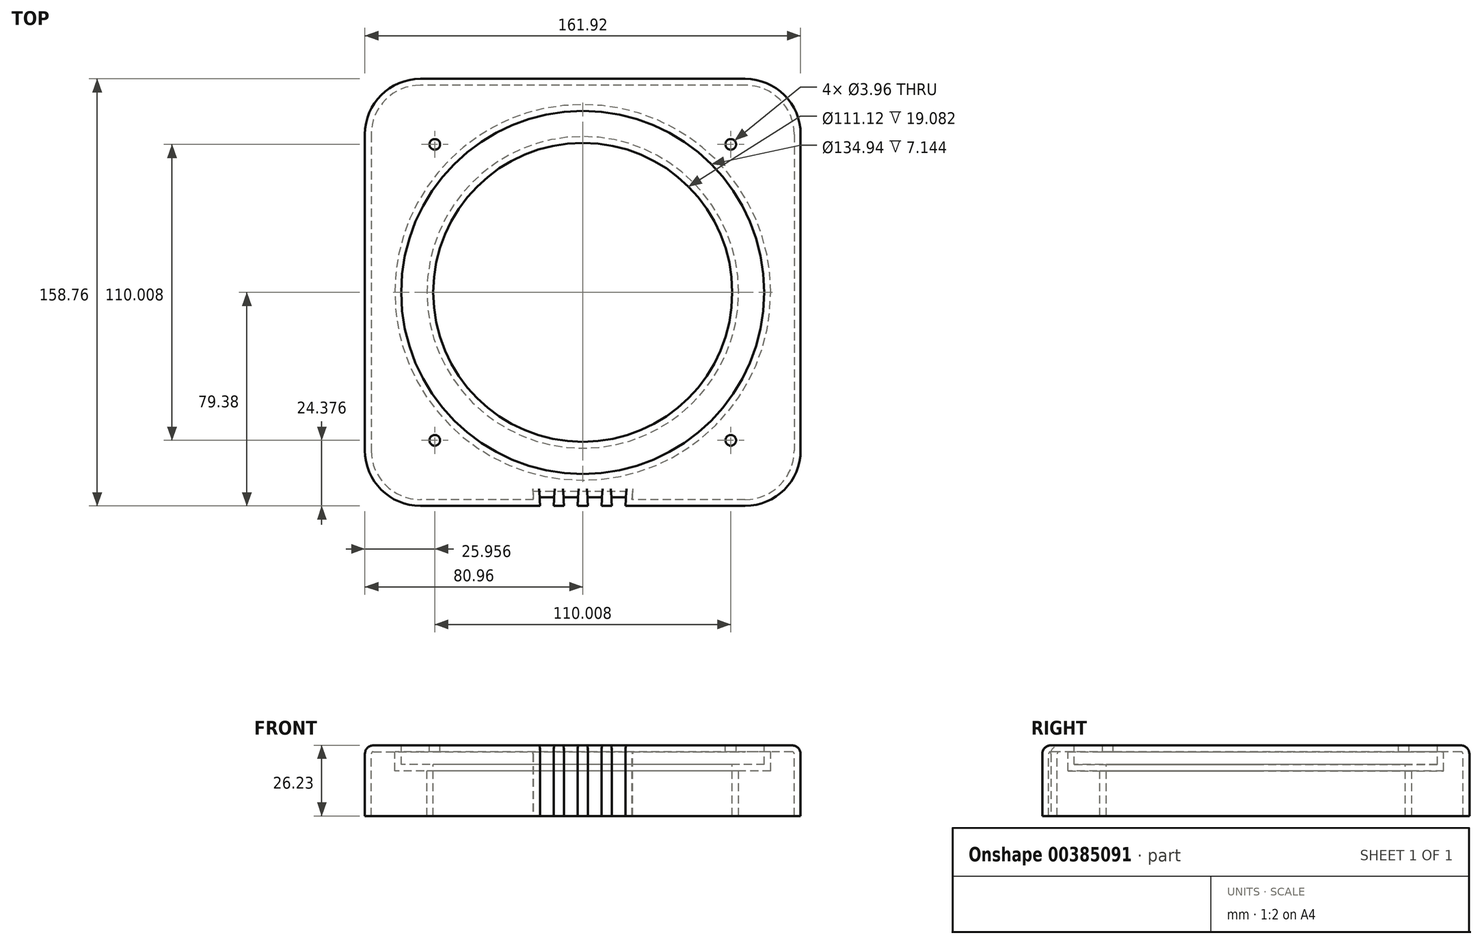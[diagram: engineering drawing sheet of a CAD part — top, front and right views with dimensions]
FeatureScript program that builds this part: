
annotation { "Feature Type Name" : "Feature", "Feature Type Description" : "" }
export const myFeature = defineFeature(function(context is Context, id is Id, definition is map)
    precondition{}
    {
        {
            var Q0;
            Q0=qCreatedBy(makeId("Top.planeOp"),FACE);
            var sketch = newSketch(context, id + "F0", { "sketchPlane" : qUnion([Q0])});
            skLineSegment(sketch, "E0.bottom", {"start": v(60.34, 79.38) * mm, "end": v(-60.34, 79.38) * mm});
            skLineSegment(sketch, "E0.top", {"start": v(60.34, -79.38) * mm, "end": v(-60.34, -79.38) * mm});
            skLineSegment(sketch, "E0.left", {"start": v(80.96, 58.75) * mm, "end": v(80.96, -58.75) * mm});
            skLineSegment(sketch, "E0.right", {"start": v(-80.96, 58.75) * mm, "end": v(-80.96, -58.75) * mm});
            skPoint(sketch, "E0.middle", {"position": v(0, 0) * mm});
            skPoint(sketch, "E1.visualSharp", {"position": v(-80.96, 79.38) * mm});
            skArc(sketch, "E1.filletArc", {"start": v(-60.34, 79.38) * mm, "mid": v(-74.92, 73.33) * mm, "end": v(-80.96, 58.75) * mm});
            skPoint(sketch, "E2.visualSharp", {"position": v(80.96, 79.38) * mm});
            skArc(sketch, "E2.filletArc", {"start": v(80.96, 58.75) * mm, "mid": v(74.92, 73.33) * mm, "end": v(60.34, 79.38) * mm});
            skPoint(sketch, "E3.visualSharp", {"position": v(80.96, -79.38) * mm});
            skArc(sketch, "E3.filletArc", {"start": v(60.34, -79.38) * mm, "mid": v(74.92, -73.33) * mm, "end": v(80.96, -58.75) * mm});
            skPoint(sketch, "E4.visualSharp", {"position": v(-80.96, -79.38) * mm});
            skArc(sketch, "E4.filletArc", {"start": v(-80.96, -58.75) * mm, "mid": v(-74.92, -73.33) * mm, "end": v(-60.34, -79.38) * mm});
            skCircle(sketch, "E5", {"center": v(0, 0) * mm, "radius": 55.56 * mm});
            skCircle(sketch, "E6", {"center": v(0, 0) * mm, "radius": 67.47 * mm});
            skCircle(sketch, "E7", {"center": v(55, 55) * mm, "radius": 1.98 * mm});
            skCircle(sketch, "E8", {"center": v(55, -55) * mm, "radius": 1.98 * mm});
            skCircle(sketch, "E9", {"center": v(-55, -55) * mm, "radius": 1.98 * mm});
            skCircle(sketch, "E10", {"center": v(-55, 55) * mm, "radius": 1.98 * mm});
            skSolve(sketch);
        }
        {
            var Q0;
            Q0=makeQuery(id+"F0.imprint","IMPRINT",FACE,{"disambiguationData":[TD([[makeQuery(id+"F0.imprint","IMPRINT",EDGE,{"derivedFrom":sQuery(id+"F0.wireOp",EDGE,"E0.bottom")}),1.0]])]});
            var Q1;
            Q1=makeQuery(id+"F0.imprint","IMPRINT",FACE,{"disambiguationData":[TD([[makeQuery(id+"F0.imprint","IMPRINT",EDGE,{"derivedFrom":sQuery(id+"F0.wireOp",EDGE,"E5")}),-1.0]])]});
            extrude(context, id + "F1", {"entities" : qUnion([Q0, Q1]), "oppositeDirection" : true, "depth" : 26.23 * mm});
        }
        {
            var Q0;
            Q0=makeQuery(id+"F1.opExtrude","SWEPT_FACE",FACE,{"disambiguationData":[OSD([sQuery(id+"F0.wireOp",EDGE,"E0.top")])]});
            var sketch = newSketch(context, id + "F2", { "sketchPlane" : qUnion([Q0])});
            skLineSegment(sketch, "E11.bottom", {"start": v(1.9, -31.75) * mm, "end": v(-1.9, -31.75) * mm});
            skLineSegment(sketch, "E11.top", {"start": v(1.9, 31.75) * mm, "end": v(-1.9, 31.75) * mm});
            skLineSegment(sketch, "E11.left", {"start": v(1.9, -31.75) * mm, "end": v(1.9, 31.75) * mm});
            skLineSegment(sketch, "E11.right", {"start": v(-1.9, -31.75) * mm, "end": v(-1.9, 31.75) * mm});
            skPoint(sketch, "E11.middle", {"position": v(0, 0) * mm});
            skLineSegment(sketch, "E12.1.0.0", {"start": v(6.98, -31.75) * mm, "end": v(6.99, 31.75) * mm});
            skLineSegment(sketch, "E12.1.0.1", {"start": v(10.8, 31.75) * mm, "end": v(6.99, 31.75) * mm});
            skLineSegment(sketch, "E12.1.0.2", {"start": v(10.8, -31.75) * mm, "end": v(10.8, 31.75) * mm});
            skLineSegment(sketch, "E12.1.0.3", {"start": v(10.8, -31.75) * mm, "end": v(6.98, -31.75) * mm});
            skLineSegment(sketch, "E12.direction1", {"start": v(-1.9, -31.75) * mm, "end": v(6.98, -31.75) * mm, "construction": true});
            skLineSegment(sketch, "E13.0.2.0", {"start": v(15.87, -31.75) * mm, "end": v(15.88, 31.75) * mm});
            skLineSegment(sketch, "E13.3.2.0", {"start": v(19.69, 31.75) * mm, "end": v(15.88, 31.75) * mm});
            skLineSegment(sketch, "E13.6.2.0", {"start": v(19.68, -31.75) * mm, "end": v(19.69, 31.75) * mm});
            skLineSegment(sketch, "E13.9.2.0", {"start": v(19.68, -31.75) * mm, "end": v(15.88, -31.75) * mm});
            skLineSegment(sketch, "E14.MirrorCS", {"start": v(-19.68, -31.75) * mm, "end": v(-15.88, -31.75) * mm});
            skLineSegment(sketch, "E15.MirrorCS", {"start": v(-10.8, -31.75) * mm, "end": v(-6.98, -31.75) * mm});
            skLineSegment(sketch, "E16.MirrorCS", {"start": v(-19.69, 31.75) * mm, "end": v(-15.88, 31.75) * mm});
            skLineSegment(sketch, "E17.MirrorCS", {"start": v(-10.8, 31.75) * mm, "end": v(-6.99, 31.75) * mm});
            skLineSegment(sketch, "E18.MirrorCS", {"start": v(-10.8, -31.75) * mm, "end": v(-10.8, 31.75) * mm});
            skLineSegment(sketch, "E19.MirrorCS", {"start": v(-19.68, -31.75) * mm, "end": v(-19.69, 31.75) * mm});
            skLineSegment(sketch, "E20.MirrorCS", {"start": v(-15.87, -31.75) * mm, "end": v(-15.88, 31.75) * mm});
            skLineSegment(sketch, "E21.MirrorCS", {"start": v(-6.98, -31.75) * mm, "end": v(-6.99, 31.75) * mm});
            skSolve(sketch);
        }
        {
            var Q0;
            Q0=makeQuery(id+"F0.imprint","IMPRINT",FACE,{"disambiguationData":[TD([[makeQuery(id+"F0.imprint","IMPRINT",EDGE,{"derivedFrom":sQuery(id+"F0.wireOp",EDGE,"E5")}),-1.0]])]});
            extrude(context, id + "F3", {"entities" : qUnion([Q0]), "operationType" : NewBodyOperationType.REMOVE, "oppositeDirection" : true, "depth" : 7.14 * mm});
        }
        {
            var Q0;
            {var subQ0=sQuery(id+"F2.wireOp",EDGE,"E18.MirrorCS");var subQ1=sQuery(id+"F0.wireOp",EDGE,"E0.top");var subQ2=makeQuery(id+"F1.opExtrude","CAP_EDGE",EDGE,{"disambiguationData":[OSD([subQ1])],"isStart":false});var subQ3=makeQuery(id+"F2.imprint","INTERSECT",VERTEX,{"derivedFrom":[subQ2,subQ0]});Q0=makeQuery(id+"F2.imprint","IMPRINT",FACE,{"disambiguationData":[TD([[makeQuery(id+"F2.imprint","IMPRINT",EDGE,{"disambiguationData":[TD([[subQ3,-1.0]])],"derivedFrom":subQ2}),-1.0]])]});}
            var Q1;
            {var subQ0=sQuery(id+"F2.wireOp",EDGE,"E11.right");var subQ1=sQuery(id+"F0.wireOp",EDGE,"E0.top");var subQ2=makeQuery(id+"F1.opExtrude","CAP_EDGE",EDGE,{"disambiguationData":[OSD([subQ1])],"isStart":false});var subQ3=makeQuery(id+"F2.imprint","INTERSECT",VERTEX,{"derivedFrom":[subQ2,subQ0]});Q1=makeQuery(id+"F2.imprint","IMPRINT",FACE,{"disambiguationData":[TD([[makeQuery(id+"F2.imprint","IMPRINT",EDGE,{"disambiguationData":[TD([[subQ3,-1.0]])],"derivedFrom":subQ2}),-1.0]])]});}
            var Q2;
            {var subQ0=sQuery(id+"F2.wireOp",EDGE,"E11.left");var subQ1=sQuery(id+"F0.wireOp",EDGE,"E0.top");var subQ2=makeQuery(id+"F1.opExtrude","CAP_EDGE",EDGE,{"disambiguationData":[OSD([subQ1])],"isStart":false});var subQ3=makeQuery(id+"F2.imprint","INTERSECT",VERTEX,{"derivedFrom":[subQ2,subQ0]});Q2=makeQuery(id+"F2.imprint","IMPRINT",FACE,{"disambiguationData":[TD([[makeQuery(id+"F2.imprint","IMPRINT",EDGE,{"disambiguationData":[TD([[subQ3,1.0]])],"derivedFrom":subQ2}),-1.0]])]});}
            var Q3;
            {var subQ0=sQuery(id+"F2.wireOp",EDGE,"E12.1.0.2");var subQ1=sQuery(id+"F0.wireOp",EDGE,"E0.top");var subQ2=makeQuery(id+"F1.opExtrude","CAP_EDGE",EDGE,{"disambiguationData":[OSD([subQ1])],"isStart":false});var subQ3=makeQuery(id+"F2.imprint","INTERSECT",VERTEX,{"derivedFrom":[subQ2,subQ0]});Q3=makeQuery(id+"F2.imprint","IMPRINT",FACE,{"disambiguationData":[TD([[makeQuery(id+"F2.imprint","IMPRINT",EDGE,{"disambiguationData":[TD([[subQ3,1.0]])],"derivedFrom":subQ2}),-1.0]])]});}
            extrude(context, id + "F4", {"entities" : qUnion([Q0, Q1, Q2, Q3]), "operationType" : NewBodyOperationType.REMOVE, "oppositeDirection" : true, "depth" : 3.17 * mm, "hasDraft" : true, "draftAngle" : 3 * degree});
        }
        {
            var Q0;
            Q0=makeQuery(id+"F1.opExtrude","CAP_EDGE",EDGE,{"disambiguationData":[OSD([sQuery(id+"F0.wireOp",EDGE,"E2.filletArc")])],"isStart":true});
            var Q1;
            Q1=makeQuery(id+"F1.opExtrude","CAP_EDGE",EDGE,{"disambiguationData":[OSD([sQuery(id+"F0.wireOp",EDGE,"E3.filletArc")])],"isStart":true});
            var Q2;
            Q2=makeQuery(id+"F1.opExtrude","CAP_EDGE",EDGE,{"disambiguationData":[OSD([sQuery(id+"F0.wireOp",EDGE,"E4.filletArc")])],"isStart":true});
            var Q3;
            Q3=makeQuery(id+"F1.opExtrude","CAP_EDGE",EDGE,{"disambiguationData":[OSD([sQuery(id+"F0.wireOp",EDGE,"E1.filletArc")])],"isStart":true});
            var Q4;
            {var subQ0=sQuery(id+"F0.wireOp",EDGE,"E0.top");var subQ1=makeQuery(id+"F1.opExtrude","CAP_EDGE",EDGE,{"disambiguationData":[OSD([subQ0])],"isStart":true});Q4=makeQuery(id+"F4.boolean.opBoolean","COPY",EDGE,{"derivedFrom":makeQuery(id+"F4.opExtrude","CAP_EDGE",EDGE,{"disambiguationData":[OSD([subQ0]),TDD([makeQuery(id+"F2.imprint","IMPRINT",EDGE,{"disambiguationData":[TD([[makeQuery(id+"F2.imprint","INTERSECT",VERTEX,{"derivedFrom":[subQ1,sQuery(id+"F2.wireOp",EDGE,"E18.MirrorCS")]}),-1.0]])],"derivedFrom":subQ1})])],"isStart":false})});}
            var Q5;
            {var subQ0=sQuery(id+"F0.wireOp",EDGE,"E0.top");Q5=makeQuery(id+"F4.boolean.opBoolean","SPLIT",EDGE,{"disambiguationData":[TD([makeQuery(id+"F4.opExtrude","SWEPT_FACE",FACE,{"disambiguationData":[OSD([sQuery(id+"F2.wireOp",EDGE,"E18.MirrorCS")])]})])],"derivedFrom":makeQuery(id+"F1.opExtrude","CAP_EDGE",EDGE,{"disambiguationData":[OSD([subQ0])],"isStart":true})});}
            var Q6;
            {var subQ0=sQuery(id+"F0.wireOp",EDGE,"E0.top");var subQ1=makeQuery(id+"F1.opExtrude","CAP_EDGE",EDGE,{"disambiguationData":[OSD([subQ0])],"isStart":true});Q6=makeQuery(id+"F4.boolean.opBoolean","COPY",EDGE,{"derivedFrom":makeQuery(id+"F4.opExtrude","CAP_EDGE",EDGE,{"disambiguationData":[OSD([subQ0]),TDD([makeQuery(id+"F2.imprint","IMPRINT",EDGE,{"disambiguationData":[TD([[makeQuery(id+"F2.imprint","INTERSECT",VERTEX,{"derivedFrom":[subQ1,sQuery(id+"F2.wireOp",EDGE,"E11.right")]}),-1.0]])],"derivedFrom":subQ1})])],"isStart":false})});}
            var Q7;
            {var subQ0=sQuery(id+"F0.wireOp",EDGE,"E0.top");Q7=makeQuery(id+"F4.boolean.opBoolean","SPLIT",EDGE,{"disambiguationData":[TD([makeQuery(id+"F4.opExtrude","SWEPT_FACE",FACE,{"disambiguationData":[OSD([sQuery(id+"F2.wireOp",EDGE,"E11.left")])]})])],"derivedFrom":makeQuery(id+"F1.opExtrude","CAP_EDGE",EDGE,{"disambiguationData":[OSD([subQ0])],"isStart":true})});}
            var Q8;
            {var subQ0=sQuery(id+"F0.wireOp",EDGE,"E0.top");var subQ1=makeQuery(id+"F1.opExtrude","CAP_EDGE",EDGE,{"disambiguationData":[OSD([subQ0])],"isStart":true});Q8=makeQuery(id+"F4.boolean.opBoolean","COPY",EDGE,{"derivedFrom":makeQuery(id+"F4.opExtrude","CAP_EDGE",EDGE,{"disambiguationData":[OSD([subQ0]),TDD([makeQuery(id+"F2.imprint","IMPRINT",EDGE,{"disambiguationData":[TD([[makeQuery(id+"F2.imprint","INTERSECT",VERTEX,{"derivedFrom":[subQ1,sQuery(id+"F2.wireOp",EDGE,"E11.left")]}),1.0]])],"derivedFrom":subQ1})])],"isStart":false})});}
            var Q9;
            {var subQ0=sQuery(id+"F0.wireOp",EDGE,"E0.top");Q9=makeQuery(id+"F4.boolean.opBoolean","SPLIT",EDGE,{"disambiguationData":[TD([makeQuery(id+"F4.opExtrude","SWEPT_FACE",FACE,{"disambiguationData":[OSD([sQuery(id+"F2.wireOp",EDGE,"E12.1.0.0")])]})])],"derivedFrom":makeQuery(id+"F1.opExtrude","CAP_EDGE",EDGE,{"disambiguationData":[OSD([subQ0])],"isStart":true})});}
            var Q10;
            {var subQ0=sQuery(id+"F0.wireOp",EDGE,"E0.top");var subQ1=makeQuery(id+"F1.opExtrude","CAP_EDGE",EDGE,{"disambiguationData":[OSD([subQ0])],"isStart":true});Q10=makeQuery(id+"F4.boolean.opBoolean","COPY",EDGE,{"derivedFrom":makeQuery(id+"F4.opExtrude","CAP_EDGE",EDGE,{"disambiguationData":[OSD([subQ0]),TDD([makeQuery(id+"F2.imprint","IMPRINT",EDGE,{"disambiguationData":[TD([[makeQuery(id+"F2.imprint","INTERSECT",VERTEX,{"derivedFrom":[subQ1,sQuery(id+"F2.wireOp",EDGE,"E12.1.0.2")]}),1.0]])],"derivedFrom":subQ1})])],"isStart":false})});}
            var Q11;
            {var subQ0=sQuery(id+"F0.wireOp",EDGE,"E0.top");Q11=makeQuery(id+"F4.boolean.opBoolean","INTERSECT",EDGE,{"derivedFrom":[makeQuery(id+"F1.opExtrude","CAP_FACE",FACE,{"disambiguationData":[OSD([sQuery(id+"F0.wireOp",EDGE,"E0.bottom"),subQ0,sQuery(id+"F0.wireOp",EDGE,"E0.left"),sQuery(id+"F0.wireOp",EDGE,"E0.right"),sQuery(id+"F0.wireOp",EDGE,"E1.filletArc"),sQuery(id+"F0.wireOp",EDGE,"E2.filletArc"),sQuery(id+"F0.wireOp",EDGE,"E3.filletArc"),sQuery(id+"F0.wireOp",EDGE,"E4.filletArc"),sQuery(id+"F0.wireOp",EDGE,"E5"),sQuery(id+"F0.wireOp",EDGE,"E7"),sQuery(id+"F0.wireOp",EDGE,"E8"),sQuery(id+"F0.wireOp",EDGE,"E9"),sQuery(id+"F0.wireOp",EDGE,"E10")])],"isStart":true}),makeQuery(id+"F4.opExtrude","CAP_FACE",FACE,{"disambiguationData":[OSD([subQ0,sQuery(id+"F2.wireOp",EDGE,"E18.MirrorCS"),sQuery(id+"F2.wireOp",EDGE,"E20.MirrorCS")])],"isStart":false})]});}
            var Q12;
            {var subQ0=sQuery(id+"F0.wireOp",EDGE,"E0.top");Q12=makeQuery(id+"F4.boolean.opBoolean","INTERSECT",EDGE,{"derivedFrom":[makeQuery(id+"F1.opExtrude","CAP_FACE",FACE,{"disambiguationData":[OSD([sQuery(id+"F0.wireOp",EDGE,"E0.bottom"),subQ0,sQuery(id+"F0.wireOp",EDGE,"E0.left"),sQuery(id+"F0.wireOp",EDGE,"E0.right"),sQuery(id+"F0.wireOp",EDGE,"E1.filletArc"),sQuery(id+"F0.wireOp",EDGE,"E2.filletArc"),sQuery(id+"F0.wireOp",EDGE,"E3.filletArc"),sQuery(id+"F0.wireOp",EDGE,"E4.filletArc"),sQuery(id+"F0.wireOp",EDGE,"E5"),sQuery(id+"F0.wireOp",EDGE,"E7"),sQuery(id+"F0.wireOp",EDGE,"E8"),sQuery(id+"F0.wireOp",EDGE,"E9"),sQuery(id+"F0.wireOp",EDGE,"E10")])],"isStart":true}),makeQuery(id+"F4.opExtrude","CAP_FACE",FACE,{"disambiguationData":[OSD([subQ0,sQuery(id+"F2.wireOp",EDGE,"E11.right"),sQuery(id+"F2.wireOp",EDGE,"E21.MirrorCS")])],"isStart":false})]});}
            var Q13;
            {var subQ0=sQuery(id+"F0.wireOp",EDGE,"E0.top");Q13=makeQuery(id+"F4.boolean.opBoolean","INTERSECT",EDGE,{"derivedFrom":[makeQuery(id+"F1.opExtrude","CAP_FACE",FACE,{"disambiguationData":[OSD([sQuery(id+"F0.wireOp",EDGE,"E0.bottom"),subQ0,sQuery(id+"F0.wireOp",EDGE,"E0.left"),sQuery(id+"F0.wireOp",EDGE,"E0.right"),sQuery(id+"F0.wireOp",EDGE,"E1.filletArc"),sQuery(id+"F0.wireOp",EDGE,"E2.filletArc"),sQuery(id+"F0.wireOp",EDGE,"E3.filletArc"),sQuery(id+"F0.wireOp",EDGE,"E4.filletArc"),sQuery(id+"F0.wireOp",EDGE,"E5"),sQuery(id+"F0.wireOp",EDGE,"E7"),sQuery(id+"F0.wireOp",EDGE,"E8"),sQuery(id+"F0.wireOp",EDGE,"E9"),sQuery(id+"F0.wireOp",EDGE,"E10")])],"isStart":true}),makeQuery(id+"F4.opExtrude","CAP_FACE",FACE,{"disambiguationData":[OSD([subQ0,sQuery(id+"F2.wireOp",EDGE,"E11.left"),sQuery(id+"F2.wireOp",EDGE,"E12.1.0.0")])],"isStart":false})]});}
            var Q14;
            {var subQ0=sQuery(id+"F0.wireOp",EDGE,"E0.top");Q14=makeQuery(id+"F4.boolean.opBoolean","INTERSECT",EDGE,{"derivedFrom":[makeQuery(id+"F1.opExtrude","CAP_FACE",FACE,{"disambiguationData":[OSD([sQuery(id+"F0.wireOp",EDGE,"E0.bottom"),subQ0,sQuery(id+"F0.wireOp",EDGE,"E0.left"),sQuery(id+"F0.wireOp",EDGE,"E0.right"),sQuery(id+"F0.wireOp",EDGE,"E1.filletArc"),sQuery(id+"F0.wireOp",EDGE,"E2.filletArc"),sQuery(id+"F0.wireOp",EDGE,"E3.filletArc"),sQuery(id+"F0.wireOp",EDGE,"E4.filletArc"),sQuery(id+"F0.wireOp",EDGE,"E5"),sQuery(id+"F0.wireOp",EDGE,"E7"),sQuery(id+"F0.wireOp",EDGE,"E8"),sQuery(id+"F0.wireOp",EDGE,"E9"),sQuery(id+"F0.wireOp",EDGE,"E10")])],"isStart":true}),makeQuery(id+"F4.opExtrude","CAP_FACE",FACE,{"disambiguationData":[OSD([subQ0,sQuery(id+"F2.wireOp",EDGE,"E12.1.0.2"),sQuery(id+"F2.wireOp",EDGE,"E13.0.2.0")])],"isStart":false})]});}
            fillet(context, id + "F5", {"entities" : qUnion([Q0, Q1, Q2, Q3, Q4, Q5, Q6, Q7, Q8, Q9, Q10, Q11, Q12, Q13, Q14]), "radius" : 3.17 * mm, "tangentPropagation" : true, "allowEdgeOverflow" : false});
        }
        {
            var Q0;
            Q0=makeQuery(id+"F1.opExtrude","CAP_FACE",FACE,{"disambiguationData":[OSD([sQuery(id+"F0.wireOp",EDGE,"E0.bottom"),sQuery(id+"F0.wireOp",EDGE,"E0.top"),sQuery(id+"F0.wireOp",EDGE,"E0.left"),sQuery(id+"F0.wireOp",EDGE,"E0.right"),sQuery(id+"F0.wireOp",EDGE,"E1.filletArc"),sQuery(id+"F0.wireOp",EDGE,"E2.filletArc"),sQuery(id+"F0.wireOp",EDGE,"E3.filletArc"),sQuery(id+"F0.wireOp",EDGE,"E4.filletArc"),sQuery(id+"F0.wireOp",EDGE,"E5"),sQuery(id+"F0.wireOp",EDGE,"E7"),sQuery(id+"F0.wireOp",EDGE,"E8"),sQuery(id+"F0.wireOp",EDGE,"E9"),sQuery(id+"F0.wireOp",EDGE,"E10")])],"isStart":false});
            shell(context, id + "F6", {"entities" : qUnion([Q0]), "thickness" : 2.36 * mm});
        }
        {
            var Q0;
            {var subQ0=sQuery(id+"F0.wireOp",EDGE,"E10");var subQ1=sQuery(id+"F0.wireOp",EDGE,"E9");var subQ2=sQuery(id+"F0.wireOp",EDGE,"E8");var subQ3=sQuery(id+"F0.wireOp",EDGE,"E7");var subQ4=sQuery(id+"F0.wireOp",EDGE,"E5");var subQ5=sQuery(id+"F0.wireOp",EDGE,"E4.filletArc");var subQ6=sQuery(id+"F0.wireOp",EDGE,"E3.filletArc");var subQ7=sQuery(id+"F0.wireOp",EDGE,"E2.filletArc");var subQ8=sQuery(id+"F0.wireOp",EDGE,"E1.filletArc");var subQ9=sQuery(id+"F0.wireOp",EDGE,"E0.right");var subQ10=sQuery(id+"F0.wireOp",EDGE,"E0.left");var subQ11=sQuery(id+"F0.wireOp",EDGE,"E0.top");var subQ12=sQuery(id+"F0.wireOp",EDGE,"E0.bottom");Q0=makeQuery(id+"F6.opShell","OFFSET_FACE",FACE,{"disambiguationData":[OSD([subQ12,subQ11,subQ10,subQ9,subQ8,subQ7,subQ6,subQ5,subQ4,subQ3,subQ2,subQ1,subQ0]),TDD([makeQuery(id+"F1.opExtrude","CAP_FACE",FACE,{"disambiguationData":[OSD([subQ12,subQ11,subQ10,subQ9,subQ8,subQ7,subQ6,subQ5,subQ4,subQ3,subQ2,subQ1,subQ0])],"isStart":false})]),OD(1.0)]});}
            var Q1;
            {var subQ0=sQuery(id+"F0.wireOp",EDGE,"E10");var subQ1=sQuery(id+"F0.wireOp",EDGE,"E9");var subQ2=sQuery(id+"F0.wireOp",EDGE,"E8");var subQ3=sQuery(id+"F0.wireOp",EDGE,"E7");var subQ4=sQuery(id+"F0.wireOp",EDGE,"E5");var subQ5=sQuery(id+"F0.wireOp",EDGE,"E4.filletArc");var subQ6=sQuery(id+"F0.wireOp",EDGE,"E3.filletArc");var subQ7=sQuery(id+"F0.wireOp",EDGE,"E2.filletArc");var subQ8=sQuery(id+"F0.wireOp",EDGE,"E1.filletArc");var subQ9=sQuery(id+"F0.wireOp",EDGE,"E0.right");var subQ10=sQuery(id+"F0.wireOp",EDGE,"E0.left");var subQ11=sQuery(id+"F0.wireOp",EDGE,"E0.top");var subQ12=sQuery(id+"F0.wireOp",EDGE,"E0.bottom");Q1=makeQuery(id+"F6.opShell","OFFSET_FACE",FACE,{"disambiguationData":[OSD([subQ12,subQ11,subQ10,subQ9,subQ8,subQ7,subQ6,subQ5,subQ4,subQ3,subQ2,subQ1,subQ0]),TDD([makeQuery(id+"F1.opExtrude","CAP_FACE",FACE,{"disambiguationData":[OSD([subQ12,subQ11,subQ10,subQ9,subQ8,subQ7,subQ6,subQ5,subQ4,subQ3,subQ2,subQ1,subQ0])],"isStart":false})]),OD(2.0)]});}
            var Q2;
            {var subQ0=sQuery(id+"F0.wireOp",EDGE,"E10");var subQ1=sQuery(id+"F0.wireOp",EDGE,"E9");var subQ2=sQuery(id+"F0.wireOp",EDGE,"E8");var subQ3=sQuery(id+"F0.wireOp",EDGE,"E7");var subQ4=sQuery(id+"F0.wireOp",EDGE,"E5");var subQ5=sQuery(id+"F0.wireOp",EDGE,"E4.filletArc");var subQ6=sQuery(id+"F0.wireOp",EDGE,"E3.filletArc");var subQ7=sQuery(id+"F0.wireOp",EDGE,"E2.filletArc");var subQ8=sQuery(id+"F0.wireOp",EDGE,"E1.filletArc");var subQ9=sQuery(id+"F0.wireOp",EDGE,"E0.right");var subQ10=sQuery(id+"F0.wireOp",EDGE,"E0.left");var subQ11=sQuery(id+"F0.wireOp",EDGE,"E0.top");var subQ12=sQuery(id+"F0.wireOp",EDGE,"E0.bottom");Q2=makeQuery(id+"F6.opShell","OFFSET_FACE",FACE,{"disambiguationData":[OSD([subQ12,subQ11,subQ10,subQ9,subQ8,subQ7,subQ6,subQ5,subQ4,subQ3,subQ2,subQ1,subQ0]),TDD([makeQuery(id+"F1.opExtrude","CAP_FACE",FACE,{"disambiguationData":[OSD([subQ12,subQ11,subQ10,subQ9,subQ8,subQ7,subQ6,subQ5,subQ4,subQ3,subQ2,subQ1,subQ0])],"isStart":false})]),OD(3.0)]});}
            var Q3;
            {var subQ0=sQuery(id+"F0.wireOp",EDGE,"E10");var subQ1=sQuery(id+"F0.wireOp",EDGE,"E9");var subQ2=sQuery(id+"F0.wireOp",EDGE,"E8");var subQ3=sQuery(id+"F0.wireOp",EDGE,"E7");var subQ4=sQuery(id+"F0.wireOp",EDGE,"E5");var subQ5=sQuery(id+"F0.wireOp",EDGE,"E4.filletArc");var subQ6=sQuery(id+"F0.wireOp",EDGE,"E3.filletArc");var subQ7=sQuery(id+"F0.wireOp",EDGE,"E2.filletArc");var subQ8=sQuery(id+"F0.wireOp",EDGE,"E1.filletArc");var subQ9=sQuery(id+"F0.wireOp",EDGE,"E0.right");var subQ10=sQuery(id+"F0.wireOp",EDGE,"E0.left");var subQ11=sQuery(id+"F0.wireOp",EDGE,"E0.top");var subQ12=sQuery(id+"F0.wireOp",EDGE,"E0.bottom");Q3=makeQuery(id+"F6.opShell","OFFSET_FACE",FACE,{"disambiguationData":[OSD([subQ12,subQ11,subQ10,subQ9,subQ8,subQ7,subQ6,subQ5,subQ4,subQ3,subQ2,subQ1,subQ0]),TDD([makeQuery(id+"F1.opExtrude","CAP_FACE",FACE,{"disambiguationData":[OSD([subQ12,subQ11,subQ10,subQ9,subQ8,subQ7,subQ6,subQ5,subQ4,subQ3,subQ2,subQ1,subQ0])],"isStart":false})]),OD(4.0)]});}
            var Q4;
            {var subQ0=sQuery(id+"F0.wireOp",EDGE,"E10");var subQ1=sQuery(id+"F0.wireOp",EDGE,"E9");var subQ2=sQuery(id+"F0.wireOp",EDGE,"E8");var subQ3=sQuery(id+"F0.wireOp",EDGE,"E7");var subQ4=sQuery(id+"F0.wireOp",EDGE,"E5");var subQ5=sQuery(id+"F0.wireOp",EDGE,"E4.filletArc");var subQ6=sQuery(id+"F0.wireOp",EDGE,"E3.filletArc");var subQ7=sQuery(id+"F0.wireOp",EDGE,"E2.filletArc");var subQ8=sQuery(id+"F0.wireOp",EDGE,"E1.filletArc");var subQ9=sQuery(id+"F0.wireOp",EDGE,"E0.right");var subQ10=sQuery(id+"F0.wireOp",EDGE,"E0.left");var subQ11=sQuery(id+"F0.wireOp",EDGE,"E0.top");var subQ12=sQuery(id+"F0.wireOp",EDGE,"E0.bottom");Q4=makeQuery(id+"F6.opShell","OFFSET_FACE",FACE,{"disambiguationData":[OSD([subQ12,subQ11,subQ10,subQ9,subQ8,subQ7,subQ6,subQ5,subQ4,subQ3,subQ2,subQ1,subQ0]),TDD([makeQuery(id+"F1.opExtrude","CAP_FACE",FACE,{"disambiguationData":[OSD([subQ12,subQ11,subQ10,subQ9,subQ8,subQ7,subQ6,subQ5,subQ4,subQ3,subQ2,subQ1,subQ0])],"isStart":true})])]});}
            extrude(context, id + "F7", {"entities" : qUnion([Q0, Q1, Q2, Q3]), "operationType" : NewBodyOperationType.REMOVE, "endBound" : BoundingType.UP_TO_SURFACE, "oppositeDirection" : true, "endBoundEntityFace" : qUnion([Q4]), "depth" : 25.4 * mm});
        }
    });
